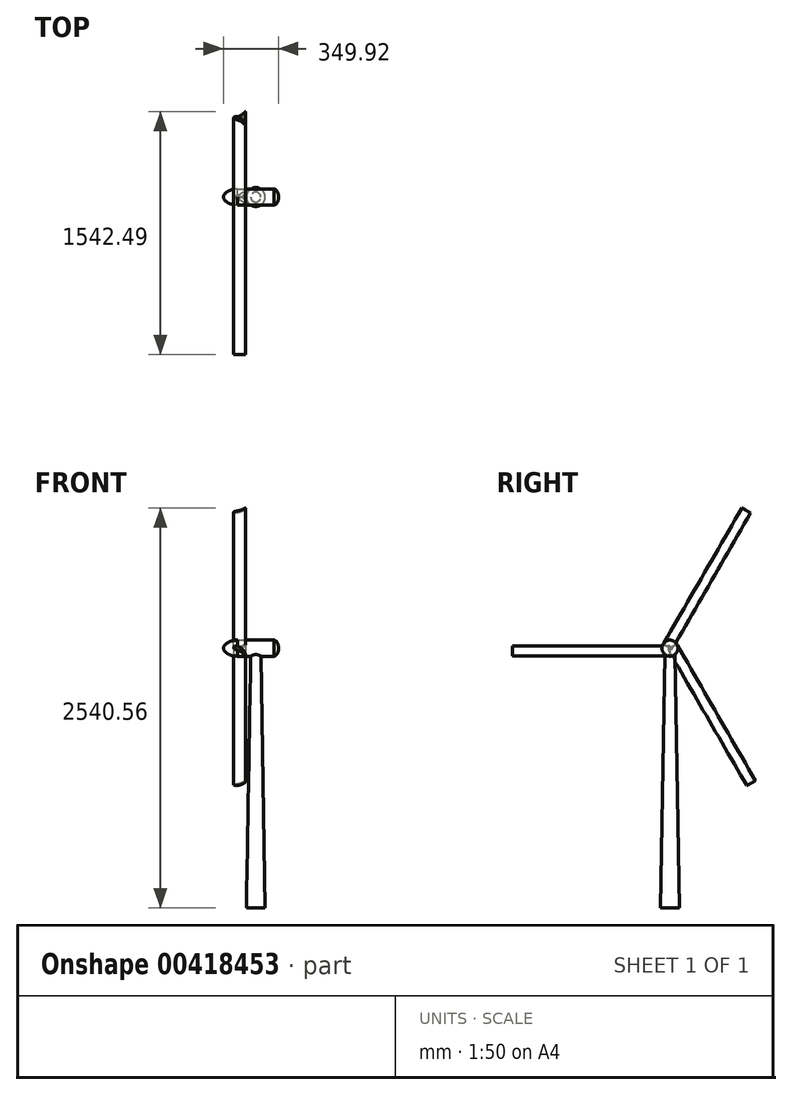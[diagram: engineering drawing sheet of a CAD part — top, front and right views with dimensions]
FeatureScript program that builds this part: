
annotation { "Feature Type Name" : "Feature", "Feature Type Description" : "" }
export const myFeature = defineFeature(function(context is Context, id is Id, definition is map)
    precondition{}
    {
        {
            var Q0;
            Q0=qCreatedBy(makeId("Front.planeOp"),FACE);
            var sketch = newSketch(context, id + "F0", { "sketchPlane" : qUnion([Q0])});
            skFitSpline(sketch, "E0", {"points": [v(-12.51, 14.38) * mm, v(-20.76, 10.73) * mm, v(-24.61, 4.95) * mm, v(-23.96, 0.28) * mm, v(-20.66, -3.84) * mm, v(-15.45, -6.86) * mm, v(-8.46, -9.51) * mm, v(4.3, -14.1) * mm, v(13.47, -18.67) * mm, v(23.1, -24.7) * mm, v(31.54, -31.44) * mm, v(40.32, -38.9) * mm, v(47.2, -47.83) * mm, v(49.08, -50) * mm, v(50.44, -50) * mm, v(52.37, -46.62) * mm, v(52.6, -41.07) * mm, v(50.44, -29.5) * mm, v(45.14, -19.38) * mm, v(31.3, -4.93) * mm, v(17.18, 6.4) * mm, v(8.02, 11.7) * mm, v(-2.58, 14.6) * mm, v(-12.51, 14.38) * mm]});
            skSolve(sketch);
        }
        {
            var Q0;
            Q0=makeQuery(id+"F0.imprint","IMPRINT",FACE,{"disambiguationData":[TD([[makeQuery(id+"F0.imprint","IMPRINT",EDGE,{"derivedFrom":sQuery(id+"F0.wireOp",EDGE,"E0")}),1.0]])]});
            extrude(context, id + "F1", {"entities" : qUnion([Q0]), "depth" : 1000 * mm, "hasDraft" : true, "draftAngle" : 0.07 * degree, "draftPullDirection" : true});
        }
        {
            var Q0;
            Q0=qCreatedBy(makeId("Top.planeOp"),FACE);
            var sketch = newSketch(context, id + "F2", { "sketchPlane" : qUnion([Q0])});
            skLineSegment(sketch, "E1", {"start": v(0, 0) * mm, "end": v(13.52, 0) * mm});
            skSolve(sketch);
        }
        {
            var Q0;
            Q0=makeQuery(id+"F1.opExtrude","SWEPT_BODY",BODY,{"disambiguationData":[OSD([sQuery(id+"F0.wireOp",EDGE,"E0")])]});
            var Q1;
            Q1=sQuery(id+"F2.wireOp",EDGE,"E1");
            circularPattern(context, id + "F3", {"entities" : qUnion([Q0]), "axis" : qUnion([Q1]), "angle" : 360 * degree, "instanceCount" : 3, "equalSpace" : true});
        }
        {
            var Q0;
            Q0=qCreatedBy(makeId("Front.planeOp"),FACE);
            var sketch = newSketch(context, id + "F4", { "sketchPlane" : qUnion([Q0])});
            skFitSpline(sketch, "E2", {"points": [v(-89.3, 0) * mm, v(-88.9, 3.45) * mm, v(-85.76, 10.54) * mm, v(-80.53, 19) * mm, v(-70.92, 28.8) * mm, v(-58.17, 37.75) * mm, v(-46.16, 43.17) * mm, v(-30.77, 47.71) * mm, v(0, 51.05) * mm], "startDerivative": vector(4.19, 91.18) * mm, "endDerivative": vector(157.3, 2.3) * mm});
            skLineSegment(sketch, "E3", {"start": v(0, 51.05) * mm, "end": v(232.15, 51.05) * mm});
            skLineSegment(sketch, "E4", {"start": v(252.41, 0) * mm, "end": v(-89.3, 0) * mm});
            skFitSpline(sketch, "E5", {"points": [v(232.15, 51.05) * mm, v(243.12, 46.98) * mm, v(250.15, 39.84) * mm, v(254.58, 33.06) * mm, v(259.27, 20.36) * mm, v(260.5, 8.16) * mm, v(260.62, 0) * mm], "startDerivative": vector(47.39, -0.57) * mm, "endDerivative": vector(2.52, -61.07) * mm});
            skLineSegment(sketch, "E6", {"start": v(252.41, 0) * mm, "end": v(260.62, 0) * mm});
            skSolve(sketch);
        }
        {
            var Q0;
            Q0=makeQuery(id+"F4.imprint","IMPRINT",FACE,{"disambiguationData":[TD([[makeQuery(id+"F4.imprint","IMPRINT",EDGE,{"derivedFrom":sQuery(id+"F4.wireOp",EDGE,"E2")}),-1.0]])]});
            var Q1;
            Q1=sQuery(id+"F4.wireOp",EDGE,"E4");
            revolve(context, id + "F5", {"entities" : qUnion([Q0]), "axis" : qUnion([Q1]), "revolveType" : RevolveType.FULL});
        }
        {
            var Q0;
            Q0=qCreatedBy(makeId("Top.planeOp"),FACE);
            var sketch = newSketch(context, id + "F6", { "sketchPlane" : qUnion([Q0])});
            skCircle(sketch, "E7", {"center": v(117.06, 0) * mm, "radius": 31.1 * mm});
            skSolve(sketch);
        }
        {
            var Q0;
            Q0 = qSketchRegion(id + "F6", true);
            extrude(context, id + "F7", {"entities" : qUnion([Q0]), "operationType" : NewBodyOperationType.ADD, "oppositeDirection" : true, "depth" : 1650 * mm, "hasDraft" : true, "draftAngle" : 1 * degree});
        }
    });
